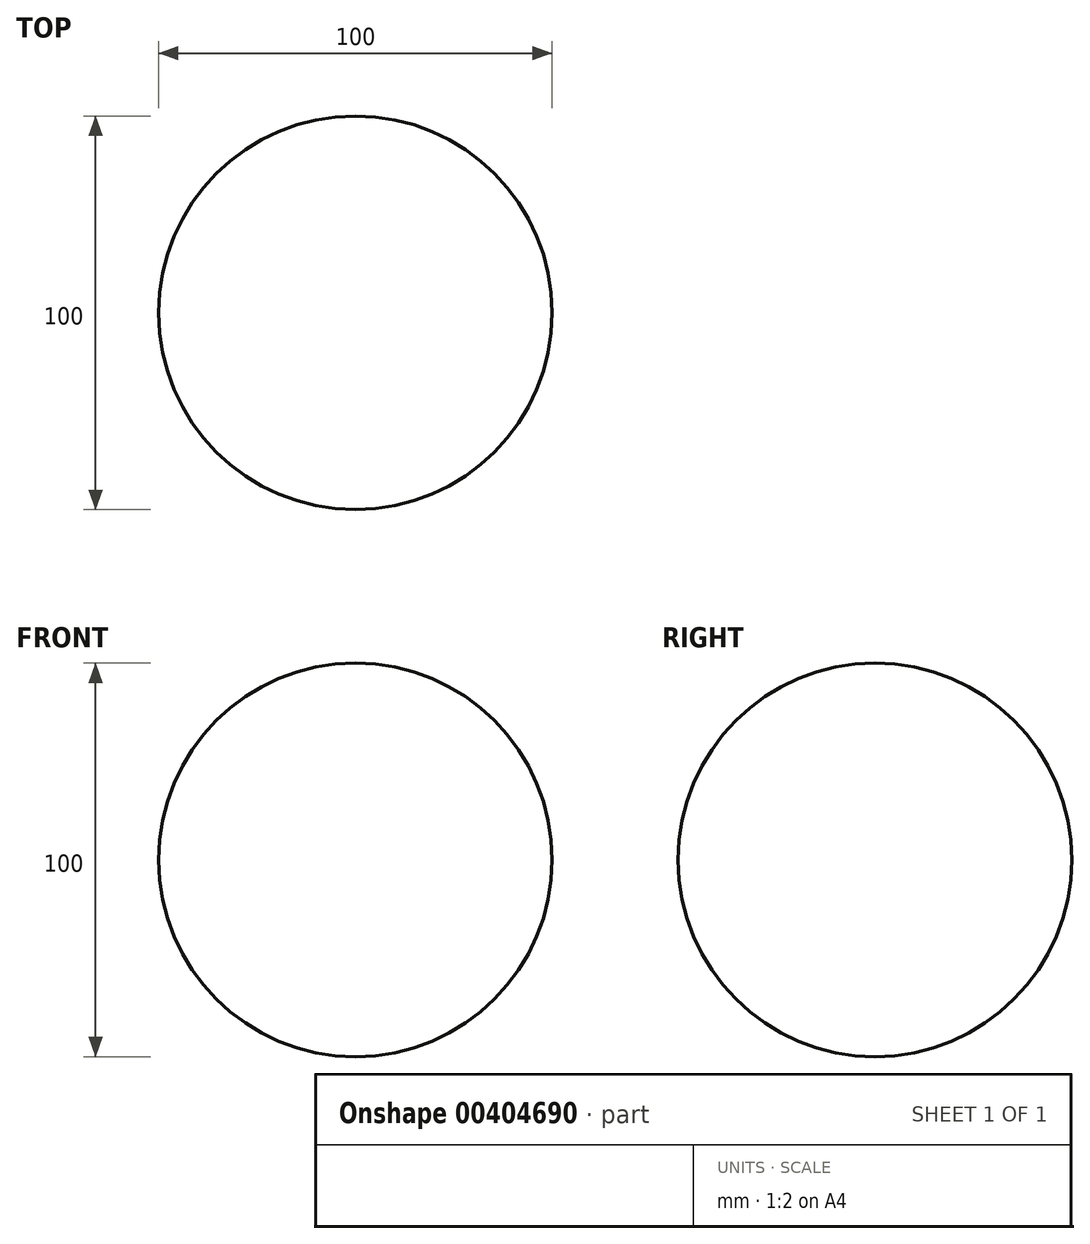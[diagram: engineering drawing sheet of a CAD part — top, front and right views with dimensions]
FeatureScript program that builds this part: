
annotation { "Feature Type Name" : "Feature", "Feature Type Description" : "" }
export const myFeature = defineFeature(function(context is Context, id is Id, definition is map)
    precondition{}
    {
        {
            var Q0;
            Q0=qCreatedBy(makeId("Front.planeOp"),FACE);
            var sketch = newSketch(context, id + "F0", { "sketchPlane" : qUnion([Q0])});
            skArc(sketch, "E0", {"start": v(0, 50) * mm, "mid": v(-50, 0) * mm, "end": v(0, -50) * mm});
            skLineSegment(sketch, "E1", {"start": v(0, 0) * mm, "end": v(0, 50) * mm, "construction": true});
            skLineSegment(sketch, "E2", {"start": v(0, 0) * mm, "end": v(0, -50) * mm, "construction": true});
            skSolve(sketch);
        }
        {
            var Q0;
            Q0=sQuery(id+"F0.wireOp",EDGE,"E0");
            var Q1;
            Q1=sQuery(id+"F0.wireOp",EDGE,"E2");
            revolve(context, id + "F1", {"bodyType" : ToolBodyType.SURFACE, "surfaceEntities" : qUnion([Q0]), "axis" : qUnion([Q1]), "revolveType" : RevolveType.FULL});
        }
    });
